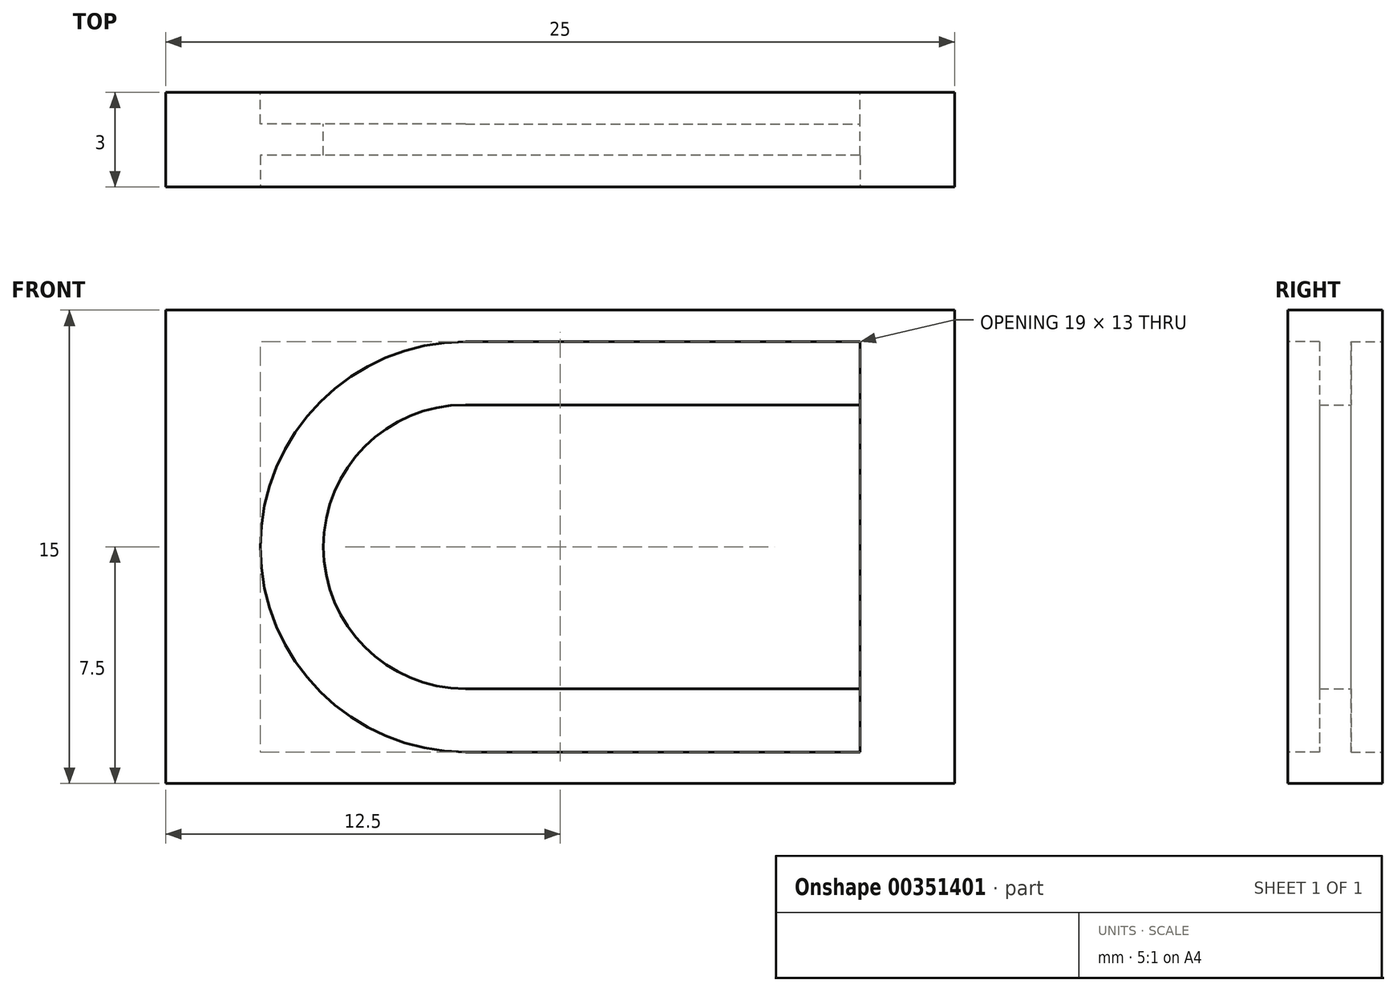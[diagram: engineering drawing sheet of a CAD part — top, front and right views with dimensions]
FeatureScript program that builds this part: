
annotation { "Feature Type Name" : "Feature", "Feature Type Description" : "" }
export const myFeature = defineFeature(function(context is Context, id is Id, definition is map)
    precondition{}
    {
        {
            var Q0;
            Q0=qCreatedBy(makeId("Front.planeOp"),FACE);
            var sketch = newSketch(context, id + "F0", { "sketchPlane" : qUnion([Q0])});
            skLineSegment(sketch, "E0.bottom", {"start": v(6.25, 4.5) * mm, "end": v(-6.25, 4.5) * mm});
            skLineSegment(sketch, "E0.top", {"start": v(6.25, -4.5) * mm, "end": v(-6.25, -4.5) * mm});
            skLineSegment(sketch, "E0.left", {"start": v(6.25, 4.5) * mm, "end": v(6.25, -4.5) * mm});
            skPoint(sketch, "E0.middle", {"position": v(0, 0) * mm});
            skArc(sketch, "E1", {"start": v(-6.25, 4.5) * mm, "mid": v(-10.75, 0) * mm, "end": v(-6.25, -4.5) * mm});
            skLineSegment(sketch, "E2", {"start": v(9.25, 7.5) * mm, "end": v(9.25, -7.5) * mm});
            skLineSegment(sketch, "E3", {"start": v(9.25, 7.5) * mm, "end": v(-13.75, 7.5) * mm});
            skLineSegment(sketch, "E4", {"start": v(9.25, -7.5) * mm, "end": v(-13.75, -7.5) * mm});
            skLineSegment(sketch, "E5.bottom", {"start": v(-13.75, 7.5) * mm, "end": v(-19.13, 7.5) * mm});
            skLineSegment(sketch, "E5.top", {"start": v(-13.75, -7.5) * mm, "end": v(-19.13, -7.5) * mm});
            skLineSegment(sketch, "E5.right", {"start": v(-19.13, 7.5) * mm, "end": v(-19.13, -7.5) * mm});
            skSolve(sketch);
        }
        {
            var Q0;
            Q0 = qSketchRegion(id + "F0", true);
            extrude(context, id + "F1", {"entities" : qUnion([Q0]), "depth" : 3 * mm});
        }
        {
            var Q0;
            Q0=makeQuery(id+"F1.opExtrude","CAP_FACE",FACE,{"disambiguationData":[OSD([sQuery(id+"F0.wireOp",EDGE,"E0.bottom"),sQuery(id+"F0.wireOp",EDGE,"E0.top"),sQuery(id+"F0.wireOp",EDGE,"E0.left"),sQuery(id+"F0.wireOp",EDGE,"E1"),sQuery(id+"F0.wireOp",EDGE,"E2"),sQuery(id+"F0.wireOp",EDGE,"E3"),sQuery(id+"F0.wireOp",EDGE,"E4"),sQuery(id+"F0.wireOp",EDGE,"E5.bottom"),sQuery(id+"F0.wireOp",EDGE,"E5.top"),sQuery(id+"F0.wireOp",EDGE,"E5.right")])],"isStart":false});
            var sketch = newSketch(context, id + "F2", { "sketchPlane" : qUnion([Q0])});
            skLineSegment(sketch, "E6.bottom", {"start": v(-6.25, 6.5) * mm, "end": v(6.25, 6.5) * mm});
            skLineSegment(sketch, "E6.top", {"start": v(-6.25, -6.5) * mm, "end": v(6.25, -6.5) * mm});
            skLineSegment(sketch, "E6.left", {"start": v(-6.25, 6.5) * mm, "end": v(-6.25, -6.5) * mm});
            skLineSegment(sketch, "E6.right", {"start": v(6.25, 6.5) * mm, "end": v(6.25, -6.5) * mm});
            skArc(sketch, "E7", {"start": v(-6.25, 6.5) * mm, "mid": v(-12.75, 0) * mm, "end": v(-6.25, -6.5) * mm});
            skSolve(sketch);
        }
        {
            var Q0;
            Q0 = qSketchRegion(id + "F2", true);
            extrude(context, id + "F3", {"entities" : qUnion([Q0]), "operationType" : NewBodyOperationType.REMOVE, "oppositeDirection" : true, "depth" : 1 * mm});
        }
        {
            var Q0;
            Q0=makeQuery(id+"F1.opExtrude","CAP_FACE",FACE,{"disambiguationData":[OSD([sQuery(id+"F0.wireOp",EDGE,"E0.bottom"),sQuery(id+"F0.wireOp",EDGE,"E0.top"),sQuery(id+"F0.wireOp",EDGE,"E0.left"),sQuery(id+"F0.wireOp",EDGE,"E1"),sQuery(id+"F0.wireOp",EDGE,"E2"),sQuery(id+"F0.wireOp",EDGE,"E3"),sQuery(id+"F0.wireOp",EDGE,"E4"),sQuery(id+"F0.wireOp",EDGE,"E5.bottom"),sQuery(id+"F0.wireOp",EDGE,"E5.top"),sQuery(id+"F0.wireOp",EDGE,"E5.right")])],"isStart":true});
            var sketch = newSketch(context, id + "F4", { "sketchPlane" : qUnion([Q0])});
            skLineSegment(sketch, "E8.bottom", {"start": v(-6.25, 6.5) * mm, "end": v(6.25, 6.5) * mm});
            skLineSegment(sketch, "E8.top", {"start": v(-6.25, -6.5) * mm, "end": v(6.25, -6.5) * mm});
            skLineSegment(sketch, "E8.left", {"start": v(-6.25, 6.5) * mm, "end": v(-6.25, -6.5) * mm});
            skLineSegment(sketch, "E8.right", {"start": v(6.25, 6.5) * mm, "end": v(6.25, -6.5) * mm});
            skArc(sketch, "E9", {"start": v(6.25, -6.5) * mm, "mid": v(12.75, 0) * mm, "end": v(6.25, 6.5) * mm});
            skSolve(sketch);
        }
        {
            var Q0;
            Q0 = qSketchRegion(id + "F4", true);
            extrude(context, id + "F5", {"entities" : qUnion([Q0]), "operationType" : NewBodyOperationType.REMOVE, "oppositeDirection" : true, "depth" : 1 * mm});
        }
        {
            var Q0;
            Q0=makeQuery(id+"F1.opExtrude","CAP_FACE",FACE,{"disambiguationData":[OSD([sQuery(id+"F0.wireOp",EDGE,"E0.bottom"),sQuery(id+"F0.wireOp",EDGE,"E0.top"),sQuery(id+"F0.wireOp",EDGE,"E0.left"),sQuery(id+"F0.wireOp",EDGE,"E1"),sQuery(id+"F0.wireOp",EDGE,"E2"),sQuery(id+"F0.wireOp",EDGE,"E3"),sQuery(id+"F0.wireOp",EDGE,"E4"),sQuery(id+"F0.wireOp",EDGE,"E5.bottom"),sQuery(id+"F0.wireOp",EDGE,"E5.top"),sQuery(id+"F0.wireOp",EDGE,"E5.right")])],"isStart":false});
            var sketch = newSketch(context, id + "F6", { "sketchPlane" : qUnion([Q0])});
            skLineSegment(sketch, "E10.bottom", {"start": v(-19.13, 7.5) * mm, "end": v(-15.75, 7.5) * mm});
            skLineSegment(sketch, "E10.top", {"start": v(-19.13, -7.5) * mm, "end": v(-15.75, -7.5) * mm});
            skLineSegment(sketch, "E10.left", {"start": v(-19.13, 7.5) * mm, "end": v(-19.13, -7.5) * mm});
            skLineSegment(sketch, "E10.right", {"start": v(-15.75, 7.5) * mm, "end": v(-15.75, -7.5) * mm});
            skSolve(sketch);
        }
        {
            var Q0;
            Q0 = qSketchRegion(id + "F6", true);
            extrude(context, id + "F7", {"entities" : qUnion([Q0]), "operationType" : NewBodyOperationType.REMOVE, "oppositeDirection" : true, "depth" : 25 * mm});
        }
    });
